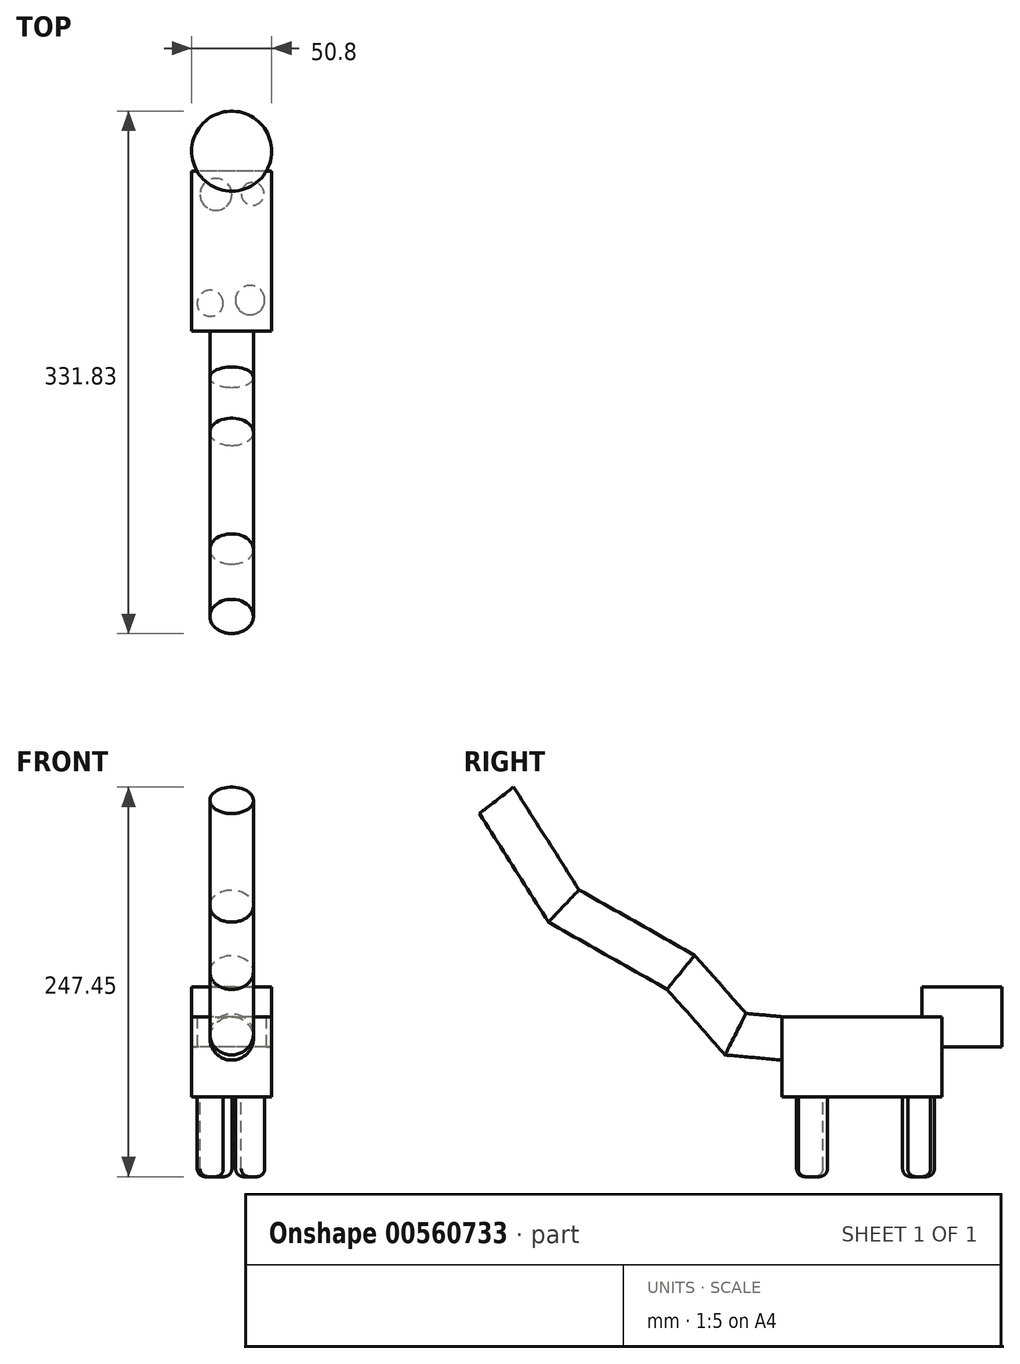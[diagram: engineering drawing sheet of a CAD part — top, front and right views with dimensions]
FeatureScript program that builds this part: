
annotation { "Feature Type Name" : "Feature", "Feature Type Description" : "" }
export const myFeature = defineFeature(function(context is Context, id is Id, definition is map)
    precondition{}
    {
        {
            var Q0;
            Q0=qCreatedBy(makeId("Top.planeOp"),FACE);
            var sketch = newSketch(context, id + "F0", { "sketchPlane" : qUnion([Q0])});
            skLineSegment(sketch, "E0.bottom", {"start": v(0, 0) * mm, "end": v(-50.8, 0) * mm});
            skLineSegment(sketch, "E0.top", {"start": v(0, 101.6) * mm, "end": v(-50.8, 101.6) * mm});
            skLineSegment(sketch, "E0.left", {"start": v(0, 0) * mm, "end": v(0, 101.6) * mm});
            skLineSegment(sketch, "E0.right", {"start": v(-50.8, 0) * mm, "end": v(-50.8, 101.6) * mm});
            skSolve(sketch);
        }
        {
            var Q0;
            Q0=makeQuery(id+"F0.imprint","IMPRINT",FACE,{"disambiguationData":[TD([[makeQuery(id+"F0.imprint","IMPRINT",EDGE,{"derivedFrom":sQuery(id+"F0.wireOp",EDGE,"E0.bottom")}),-1.0]])]});
            extrude(context, id + "F1", {"entities" : qUnion([Q0]), "depth" : 50.8 * mm, "offsetDistance" : 25.4 * mm});
        }
        {
            var Q0;
            Q0=makeQuery(id+"F1.opExtrude","CAP_FACE",FACE,{"disambiguationData":[OSD([sQuery(id+"F0.wireOp",EDGE,"E0.bottom"),sQuery(id+"F0.wireOp",EDGE,"E0.top"),sQuery(id+"F0.wireOp",EDGE,"E0.left"),sQuery(id+"F0.wireOp",EDGE,"E0.right")])],"isStart":false});
            var sketch = newSketch(context, id + "F2", { "sketchPlane" : qUnion([Q0])});
            skLineSegment(sketch, "E1", {"start": v(-25.4, 101.6) * mm, "end": v(-25.4, 114.3) * mm});
            skCircle(sketch, "E2", {"center": v(-25.4, 114.3) * mm, "radius": 25.4 * mm});
            skSolve(sketch);
        }
        {
            var Q0;
            {var subQ1=makeQuery(id+"F1.opExtrude","CAP_EDGE",EDGE,{"disambiguationData":[OSD([sQuery(id+"F0.wireOp",EDGE,"E0.top")])],"isStart":false});var subQ4=makeQuery(id+"F2.imprint","IMPRINT",VERTEX,{"derivedFrom":subQ1});Q0=makeQuery(id+"F2.imprint","IMPRINT",FACE,{"disambiguationData":[TD([[makeQuery(id+"F2.imprint","IMPRINT",EDGE,{"disambiguationData":[TD([[subQ4,1.0]])],"derivedFrom":subQ1}),1.0]])]});}
            var Q1;
            {var subQ1=makeQuery(id+"F1.opExtrude","CAP_EDGE",EDGE,{"disambiguationData":[OSD([sQuery(id+"F0.wireOp",EDGE,"E0.top")])],"isStart":false});var subQ4=makeQuery(id+"F2.imprint","IMPRINT",VERTEX,{"derivedFrom":subQ1});Q1=makeQuery(id+"F2.imprint","IMPRINT",FACE,{"disambiguationData":[TD([[makeQuery(id+"F2.imprint","IMPRINT",EDGE,{"disambiguationData":[TD([[subQ4,1.0]])],"derivedFrom":subQ1}),-1.0]])]});}
            extrude(context, id + "F3", {"entities" : qUnion([Q0, Q1]), "operationType" : NewBodyOperationType.ADD, "endBound" : BoundingType.SYMMETRIC, "depth" : 38.1 * mm, "offsetDistance" : 25.4 * mm});
        }
        {
            var Q0;
            Q0=makeQuery(id+"F1.opExtrude","CAP_FACE",FACE,{"disambiguationData":[OSD([sQuery(id+"F0.wireOp",EDGE,"E0.bottom"),sQuery(id+"F0.wireOp",EDGE,"E0.top"),sQuery(id+"F0.wireOp",EDGE,"E0.left"),sQuery(id+"F0.wireOp",EDGE,"E0.right")])],"isStart":true});
            var sketch = newSketch(context, id + "F4", { "sketchPlane" : qUnion([Q0])});
            skCircle(sketch, "E3", {"center": v(-38.99, -17.68) * mm, "radius": 8.29 * mm});
            skCircle(sketch, "E4", {"center": v(-13.67, -19.7) * mm, "radius": 9.28 * mm});
            skCircle(sketch, "E5", {"center": v(-35.37, -86.82) * mm, "radius": 10.08 * mm});
            skCircle(sketch, "E6", {"center": v(-12.06, -87.22) * mm, "radius": 7.23 * mm});
            skSolve(sketch);
        }
        {
            var Q0;
            Q0=makeQuery(id+"F4.imprint","IMPRINT",FACE,{"disambiguationData":[TD([[makeQuery(id+"F4.imprint","IMPRINT",EDGE,{"derivedFrom":sQuery(id+"F4.wireOp",EDGE,"E3")}),1.0]])]});
            var Q1;
            Q1=makeQuery(id+"F4.imprint","IMPRINT",FACE,{"disambiguationData":[TD([[makeQuery(id+"F4.imprint","IMPRINT",EDGE,{"derivedFrom":sQuery(id+"F4.wireOp",EDGE,"E4")}),1.0]])]});
            var Q2;
            Q2=makeQuery(id+"F4.imprint","IMPRINT",FACE,{"disambiguationData":[TD([[makeQuery(id+"F4.imprint","IMPRINT",EDGE,{"derivedFrom":sQuery(id+"F4.wireOp",EDGE,"E5")}),1.0]])]});
            var Q3;
            Q3=makeQuery(id+"F4.imprint","IMPRINT",FACE,{"disambiguationData":[TD([[makeQuery(id+"F4.imprint","IMPRINT",EDGE,{"derivedFrom":sQuery(id+"F4.wireOp",EDGE,"E6")}),1.0]])]});
            extrude(context, id + "F5", {"entities" : qUnion([Q0, Q1, Q2, Q3]), "operationType" : NewBodyOperationType.ADD, "depth" : 50.8 * mm, "offsetDistance" : 25.4 * mm});
        }
        {
            var Q0;
            Q0=makeQuery(id+"F5.opExtrude","CAP_EDGE",EDGE,{"disambiguationData":[OSD([sQuery(id+"F4.wireOp",EDGE,"E5")])],"isStart":false});
            var Q1;
            Q1=makeQuery(id+"F5.opExtrude","CAP_EDGE",EDGE,{"disambiguationData":[OSD([sQuery(id+"F4.wireOp",EDGE,"E6")])],"isStart":false});
            var Q2;
            Q2=makeQuery(id+"F5.opExtrude","CAP_EDGE",EDGE,{"disambiguationData":[OSD([sQuery(id+"F4.wireOp",EDGE,"E3")])],"isStart":false});
            var Q3;
            Q3=makeQuery(id+"F5.opExtrude","CAP_EDGE",EDGE,{"disambiguationData":[OSD([sQuery(id+"F4.wireOp",EDGE,"E4")])],"isStart":false});
            fillet(context, id + "F6", {"entities" : qUnion([Q0, Q1, Q2, Q3]), "radius" : 5.08 * mm, "tangentPropagation" : true, "allowEdgeOverflow" : false});
        }
        {
            var Q0;
            Q0=qCreatedBy(makeId("Right.planeOp"),FACE);
            var sketch = newSketch(context, id + "F7", { "sketchPlane" : qUnion([Q0])});
            skLineSegment(sketch, "E7", {"start": v(0, 7.94) * mm, "end": v(-43.44, 11.92) * mm});
            skLineSegment(sketch, "E8", {"start": v(-43.44, 11.92) * mm, "end": v(-82.6, 56.19) * mm});
            skLineSegment(sketch, "E9", {"start": v(-82.6, 56.19) * mm, "end": v(-159.09, 99.52) * mm});
            skLineSegment(sketch, "E10", {"start": v(-159.09, 99.52) * mm, "end": v(-204.23, 170.44) * mm});
            skSolve(sketch);
        }
        {
            var Q0;
            Q0=makeQuery(id+"F1.opExtrude","SWEPT_FACE",FACE,{"disambiguationData":[OSD([sQuery(id+"F0.wireOp",EDGE,"E0.bottom")])]});
            var sketch = newSketch(context, id + "F8", { "sketchPlane" : qUnion([Q0])});
            skCircle(sketch, "E11", {"center": v(-25.4, 37.02) * mm, "radius": 13.78 * mm});
            skPoint(sketch, "E11.centerSnap0", {"position": v(-25.4, 50.8) * mm});
            skSolve(sketch);
        }
        {
            var Q0;
            Q0=makeQuery(id+"F8.imprint","IMPRINT",FACE,{"disambiguationData":[TD([[makeQuery(id+"F8.imprint","IMPRINT",EDGE,{"derivedFrom":sQuery(id+"F8.wireOp",EDGE,"E11")}),1.0]])]});
            var Q1;
            Q1=sQuery(id+"F7.wireOp",EDGE,"E7");
            var Q2;
            Q2=sQuery(id+"F7.wireOp",EDGE,"E8");
            var Q3;
            Q3=sQuery(id+"F7.wireOp",EDGE,"E9");
            var Q4;
            Q4=sQuery(id+"F7.wireOp",EDGE,"E10");
            sweep(context, id + "F9", {"operationType" : NewBodyOperationType.ADD, "profiles" : qUnion([Q0]), "path" : qUnion([Q1, Q2, Q3, Q4])});
        }
    });
